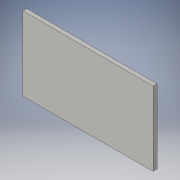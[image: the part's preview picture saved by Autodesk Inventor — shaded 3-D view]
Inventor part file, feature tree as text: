
AUTODESK INVENTOR PART (.ipt)
format: ipt  version: 2016 (Build 200138000, 138)  size: 89,600 bytes
history: native  units: in
note: dims shown in document units (in); Inventor stores cm internally (conversion verified against a paired STEP export)
features: extrude x1, sketch x1
ambient origin geometry x8: Origin, YZ Plane, XZ Plane, XY Plane, X Axis, Y Axis, Z Axis, Center Point
bodies: Solid1 (feature_tree)
feature tree (2):
  extrude  "Extrusion1"  Depth=9.375in
  sketch  "Sketch1"  dims[d0=16.5in d1=9.375in d2=0.5in d3=0.0in]
